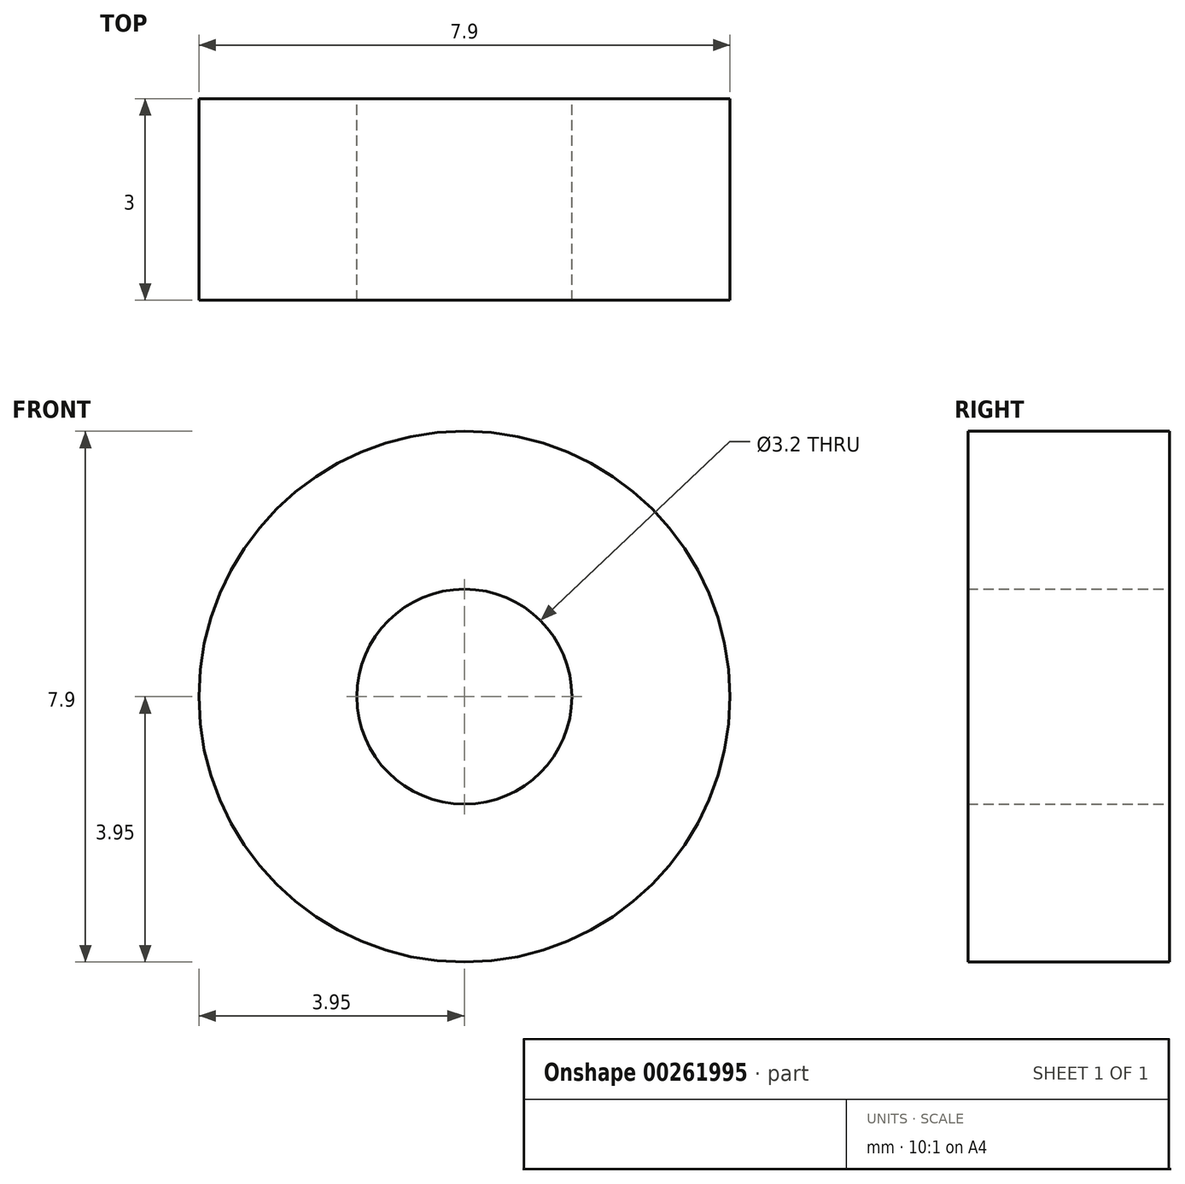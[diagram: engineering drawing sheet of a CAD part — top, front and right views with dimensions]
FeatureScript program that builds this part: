
annotation { "Feature Type Name" : "Feature", "Feature Type Description" : "" }
export const myFeature = defineFeature(function(context is Context, id is Id, definition is map)
    precondition{}
    {
        {
            assignVariable(context, id + "F0", {"name" : "Hieght", "anyValue" : 3});
        }
        {
            var Q0;
            Q0=qCreatedBy(makeId("Front.planeOp"),FACE);
            var sketch = newSketch(context, id + "F1", { "sketchPlane" : qUnion([Q0])});
            skCircle(sketch, "E0", {"center": v(0, 0) * mm, "radius": 1.6 * mm});
            skCircle(sketch, "E1", {"center": v(0, 0) * mm, "radius": 3.95 * mm});
            skSolve(sketch);
        }
        {
            var Q0;
            Q0=makeQuery(id+"F1.imprint","IMPRINT",FACE,{"disambiguationData":[TD([[makeQuery(id+"F1.imprint","IMPRINT",EDGE,{"derivedFrom":sQuery(id+"F1.wireOp",EDGE,"E0")}),-1.0]])]});
            extrude(context, id + "F2", {"entities" : qUnion([Q0]), "depth" : getVariable(context, 'Hieght') * mm});
        }
    });
